# Revit family: Lighting-Industriale-GEWISS-SMART[4]HE_APPARECCHI-LED_4M_DALI
name_source: partatom
category: Apparecchi per illuminazione
units: mm (PartAtom-declared; Revit-internal decimal feet)

## family parameters
Basato su piano di lavoro = Sì
Condiviso = No
Numero OmniClass = 23.80.70.00
Punto di calcolo locali = No
Quota connettore circolare = Usa diametro
Sempre verticale = No
Sorgente d'illuminazione = No
Taglio con vuoti quando caricato = No
Tipo di parte = Normale
Titolo OmniClass = Lighting

## types (1)
- Lighting-Industriale-GEWISS-SMART[4]HE_APPARECCHI-LED_4M_DALI
    Alimentatore = Incluso
    Apparecchio a ridotta temperatura superficiale = Si
    Applicazione = Interno
    Cablaggio = Con connettore stagno Gw connect
    Caratteristiche elettriche e gestione della luce = -
    Caratteristiche ottiche e illuminotecniche = -
    Carico apparente = 194 VA
    Catalogo = LIGHTING
    Certificazione DIN 18032-3 = Con Staffa - Kit Funi + morsetto (in approvazione)
    Certificazioni e classificazioni = -
    Classe fotobiologica = RG0
    Classe isolamento = I
    Classificazione = Lighting
    Classificazione: = -
    Codice Electrocod = 2444
    Codice digitale univoco (Datamatrix) = Datamatrix
    Colore = Grigio RAL 7035
    Commenti sul wattaggio = 194W
    Contesto = Illuminazione di industrie e impianti sportivi di grandi dimensioni
    Controllo abbagliamento e luminanza = -
    Corpo = PA6 “Halogen Free” caricato fibra vetro
    Descrizione = SMART[4]HB 4M C.PAS.DALI ELL.57K
    Dispositivo di protezione = DM 6 kV / CM 10 kV
    Distanza Sorg_Lum = 21 mm
    Durata di vita = L90B10 (Tq+25°C) = 100.000 h - L90B10 (Tq+50°C) = 50.000 h
    Efficienza luminosa (lm/W) = 133
    Finitura colore = Grigio RAL 7035
    Fissaggio = -
    Frequenza nominale (Hz) = 50/60 Hz
    Gancio di chiusura = -
    Garanzia = 5 anni
    Grado di protezione = IP66
    Gruppo ottico = Riflettore in PC metallizzato e lenti in PMMA
    Guarnizioni = tipo siliconico antinvecchiamento
    IDF = 714807ad-973c-443e-97dc-ae7f07b51596
    IDT = a901a3df6c4a4f48b998655520b49dfe
    IPEA = -
    Immagine tipo = GWL1371.jpg
    Inclinazione = Con accessorio staffa
    Indice di resa cromatica = CRI-80
    Informazioni generali = -
    Installazione e manutenzione = -
    Lampada = LED
    Larghezza = 504 mm  [stored 1.65354 ft]
    Lumen output (lm) = 25100
    Lunghezza = 700 mm  [stored 2.29659 ft]
    Materiali = -
    Modello = GWS4423AQ857
    Norma di riferimento = EN 60598-1 ; EN 60598-2-1 ; EN 60598-2-24
    Ottica = Ellittica
    Peso (kg): = 13,5
    Potenza di sistema = 189W
    Produttore = GEWISS S.p.A.
    Prospetto di default = 1219 mm
    Resistenza agli urti = IK08
    Resistenza al filo incandescente = 850 °C
    SEO = High bay
    Scheda Tecnica = https://www.gewiss.com
    Schermo = Vetro Temprato Spessore 4mm
    Sistema di controllo = 1 x DALI DT6
    Sistema di controllo : = DALI
    Sostituibilità gruppo ottico = Non sostituibile
    Sostituibilità piastra di cablaggio = Non sostituibile
    Spessore plafoniera = 40 mm  [stored 0.131234 ft]
    Superficie massima esposta al vento : = 0,350 m²
    Temperatura di colore = 5700K
    Temperatura di esercizio = -30°C ÷ +50 °C
    Temperatura di stoccaggio = -40 +70 °C
    Tensione di alimentazione = 220 - 240 V
    Tipo di apparecchio = Riflettore industriale a LED&nbsp;
    Tipo di installazione e montaggio = Plafone - Parete - Sospensione
    Tipologia sorgente luminosa = LED - Non sostituibile
    Tolleranza cromatica = SDCM = 3
    URL = https://www.gewiss.com
    Vano di alimentazione = Integrato
    Versione file RFA = 20.11
    Viti esterne = Acciaio inox
    Voltaggio = 230 V

note: [stored X ft] marks values corroborated as IEEE doubles in the binary element streams (Revit-internal decimal feet)

## geometry (parser evidence)
native form markers: Sweep x1
no freeform markers — native parametric forms only
